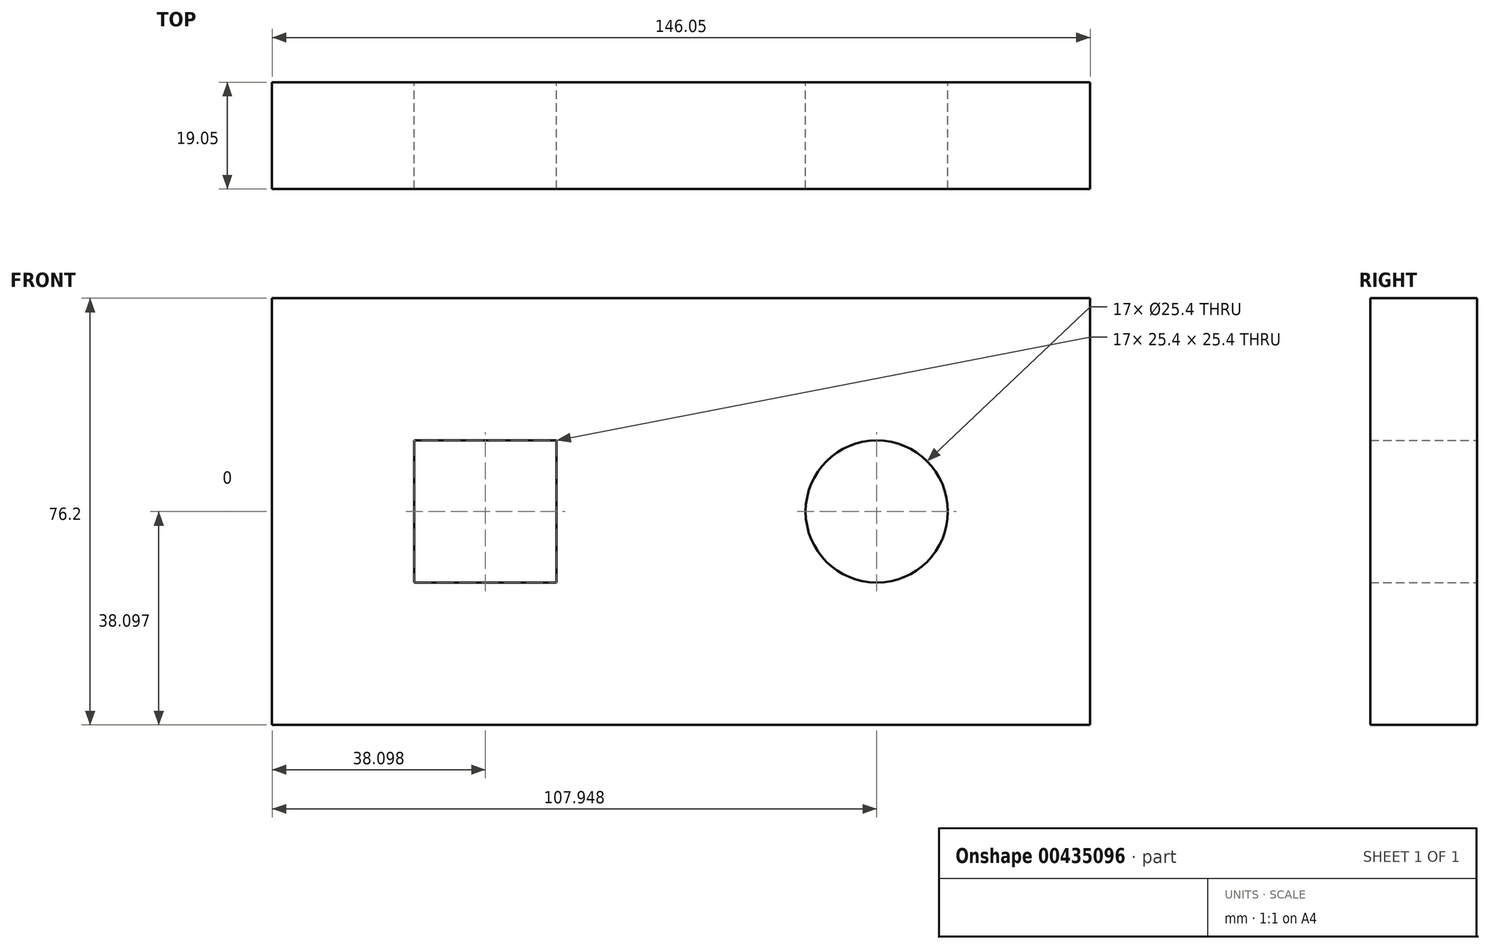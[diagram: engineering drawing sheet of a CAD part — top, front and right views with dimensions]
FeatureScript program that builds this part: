
annotation { "Feature Type Name" : "Feature", "Feature Type Description" : "" }
export const myFeature = defineFeature(function(context is Context, id is Id, definition is map)
    precondition{}
    {
        {
            var Q0;
            Q0=qCreatedBy(makeId("Front.planeOp"),FACE);
            var sketch = newSketch(context, id + "F0", { "sketchPlane" : qUnion([Q0])});
            skLineSegment(sketch, "E0", {"start": v(-74.47, 15.67) * mm, "end": v(-74.47, -60.53) * mm});
            skLineSegment(sketch, "E1", {"start": v(-74.47, -60.53) * mm, "end": v(71.58, -60.53) * mm});
            skLineSegment(sketch, "E2", {"start": v(71.58, -60.53) * mm, "end": v(71.58, 15.67) * mm});
            skLineSegment(sketch, "E3", {"start": v(71.58, 15.67) * mm, "end": v(-74.47, 15.67) * mm});
            skLineSegment(sketch, "E4.bottom", {"start": v(-49.07, -9.73) * mm, "end": v(-23.67, -9.73) * mm});
            skLineSegment(sketch, "E4.top", {"start": v(-49.07, -35.13) * mm, "end": v(-23.67, -35.13) * mm});
            skLineSegment(sketch, "E4.left", {"start": v(-49.07, -9.73) * mm, "end": v(-49.07, -35.13) * mm});
            skLineSegment(sketch, "E4.right", {"start": v(-23.67, -9.73) * mm, "end": v(-23.67, -35.13) * mm});
            skCircle(sketch, "E5", {"center": v(33.48, -22.43) * mm, "radius": 12.7 * mm});
            skSolve(sketch);
        }
        {
            var Q0;
            Q0 = qSketchRegion(id + "F0", true);
            extrude(context, id + "F1", {"entities" : qUnion([Q0]), "depth" : 19.05 * mm});
        }
    });
